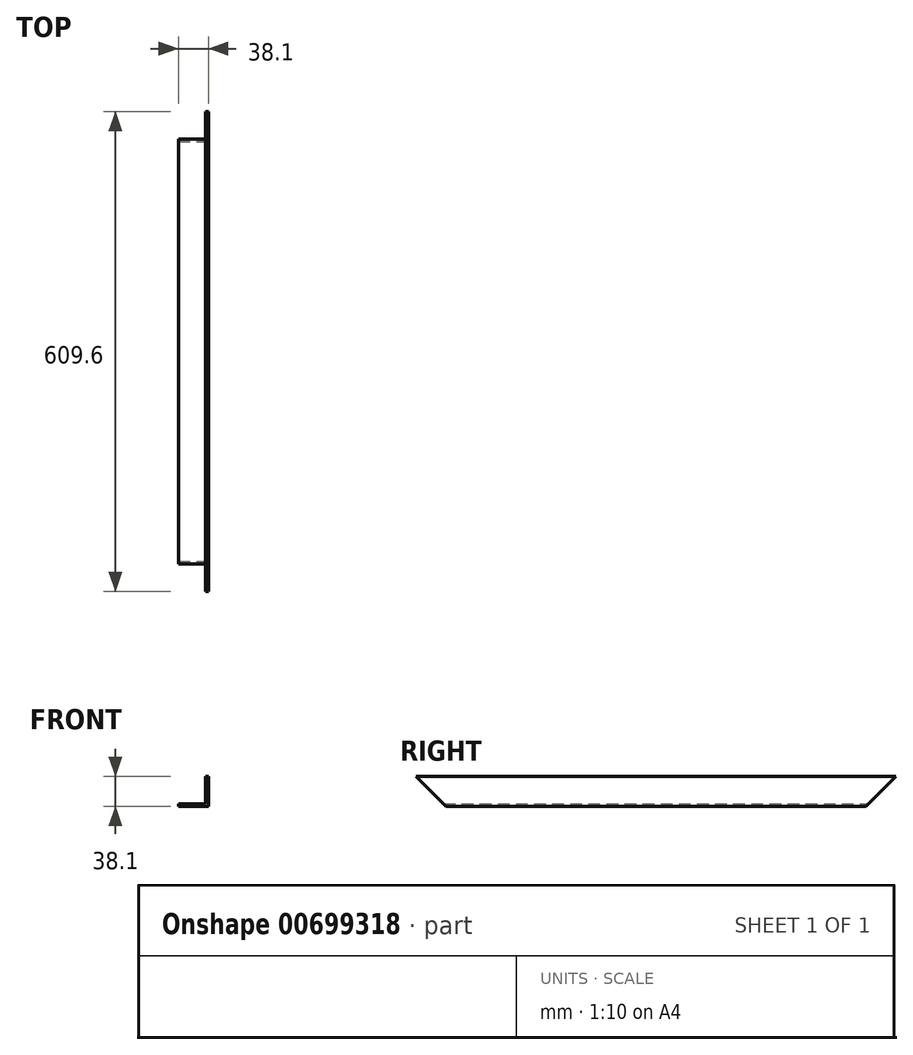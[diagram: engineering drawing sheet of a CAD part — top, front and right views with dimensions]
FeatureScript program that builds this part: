
annotation { "Feature Type Name" : "Feature", "Feature Type Description" : "" }
export const myFeature = defineFeature(function(context is Context, id is Id, definition is map)
    precondition{}
    {
        {
            var Q0;
            Q0=qCreatedBy(makeId("Front.planeOp"),FACE);
            var sketch = newSketch(context, id + "F0", { "sketchPlane" : qUnion([Q0])});
            skLineSegment(sketch, "E0", {"start": v(0, 0) * mm, "end": v(38.1, 0) * mm});
            skLineSegment(sketch, "E1", {"start": v(38.1, 0) * mm, "end": v(38.1, 38.1) * mm});
            skLineSegment(sketch, "E2", {"start": v(38.1, 38.1) * mm, "end": v(34.93, 38.1) * mm});
            skLineSegment(sketch, "E3", {"start": v(34.93, 38.1) * mm, "end": v(34.93, 3.18) * mm});
            skLineSegment(sketch, "E4", {"start": v(34.93, 3.18) * mm, "end": v(0, 3.18) * mm});
            skLineSegment(sketch, "E5", {"start": v(0, 3.18) * mm, "end": v(0, 0) * mm});
            skSolve(sketch);
        }
        {
            var Q0;
            Q0=makeQuery(id+"F0.imprint","IMPRINT",FACE,{"disambiguationData":[TD([[makeQuery(id+"F0.imprint","IMPRINT",EDGE,{"derivedFrom":sQuery(id+"F0.wireOp",EDGE,"E0")}),1.0]])]});
            extrude(context, id + "F1", {"entities" : qUnion([Q0]), "depth" : 609.6 * mm, "offsetDistance" : 25.4 * mm});
        }
        {
            var Q0;
            Q0=makeQuery(id+"F1.opExtrude","SWEPT_FACE",FACE,{"disambiguationData":[OSD([sQuery(id+"F0.wireOp",EDGE,"E1")])]});
            var sketch = newSketch(context, id + "F2", { "sketchPlane" : qUnion([Q0])});
            skLineSegment(sketch, "E6", {"start": v(-609.6, 38.1) * mm, "end": v(-571.5, 0) * mm});
            skLineSegment(sketch, "E7", {"start": v(-571.5, 0) * mm, "end": v(-609.6, 0) * mm});
            skLineSegment(sketch, "E8", {"start": v(-609.6, 0) * mm, "end": v(-609.6, 38.1) * mm});
            skLineSegment(sketch, "E9", {"start": v(0, 38.1) * mm, "end": v(-38.1, 0) * mm});
            skLineSegment(sketch, "E10", {"start": v(-38.1, 0) * mm, "end": v(0, 0) * mm});
            skLineSegment(sketch, "E11", {"start": v(0, 0) * mm, "end": v(0, 38.1) * mm});
            skSolve(sketch);
        }
        {
            var Q0;
            Q0=makeQuery(id+"F2.imprint","IMPRINT",FACE,{"disambiguationData":[TD([[makeQuery(id+"F2.imprint","IMPRINT",EDGE,{"derivedFrom":sQuery(id+"F2.wireOp",EDGE,"E9")}),1.0]])]});
            var Q1;
            Q1=makeQuery(id+"F2.imprint","IMPRINT",FACE,{"disambiguationData":[TD([[makeQuery(id+"F2.imprint","IMPRINT",EDGE,{"derivedFrom":sQuery(id+"F2.wireOp",EDGE,"E6")}),-1.0]])]});
            extrude(context, id + "F3", {"entities" : qUnion([Q0, Q1]), "operationType" : NewBodyOperationType.REMOVE, "endBound" : BoundingType.THROUGH_ALL, "oppositeDirection" : true, "depth" : 25.4 * mm, "offsetDistance" : 25.4 * mm});
        }
    });
